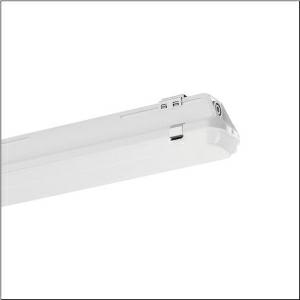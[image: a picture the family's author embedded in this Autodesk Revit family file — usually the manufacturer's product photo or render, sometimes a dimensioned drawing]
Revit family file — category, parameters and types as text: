
# Revit family: monsun_r__11_51fp108p460h_7b9f
name_source: partatom
category: Lighting Fixtures
units: mm (PartAtom-declared; Revit-internal decimal feet)

## family parameters
Cut with Voids When Loaded = No
Host = Face
Light Source = No
Part Type = Normal
Room Calculation Point = No
Round Connector Dimension = Use Diameter
Shared = No

## types (1)
- Monsun® 11 (1 x LED, 6100 lm, 33.9 W, 4000K)
    Apparent Load = 34 VA
    CIE Flux Codes = 47 77 93 94 100
    Color Rendering = 80
    Color Temperature = 4000K
    Default Elevation = 1800 mm
    Description = Monsun® 11, damp-proof luminaire, chain hanger, primary optical cover: enclosure, of PMMA, light emission: direct distribution, primary light characteristic: symmetric, installation type: suspended mounting, surface-mounted, horizontal mounting, vertical mounting, LED, rated luminous flux: 6.100lm, luminous efficacy: 180lm/W, light colour: 840, colour temperature: 4000K, control gear: ON/OFF, with terminal, 3-pole, max. 2.5mm², mains connection: 220..240V, AC, 50/60Hz, rated input power: 34W, luminaire housing, of glass-fibre reinforced polyester, uncoated, bright grey, incl. chain hanger, length: 1.590mm, width: 90mm, height: 88mm, clip for enclosure, of stainless steel (V2A), ceiling mounting element, of stainless steel (V2A), chain hanger, of stainless steel (V2A), protection rating (complete): IP66, insulation class (complete): insulation class I (protective earthing), certification: CE, ENEC, VDE, UKCA, protection symbol: D, impact resistance: IK04, permissible operating ambient temperature: -35..+40°C, standard: EN 50419, EN 60598-2-1, no direct snow, no direct sun, no direct rain, for indoor or canopied outdoor use, corresponds to IFS (International Featured Standards) requirements for safety and quality in the food industry, contact your sales advisor before using the luminaires in applications with unclear chemical exposure, large temperature fluctuations or condensation-forming humidity, LABS conformity tested according to VDMA 24364:2018-05, packaging unit: 1 piece
    Height = 89 mm
    Lamp = 1 x LED
    Lamp Light Flux = 6100 lm
    Lamp Power = 33.9 W
    Lamp count = 1
    Length = 1590 mm
    Luminous efficacy = 180 lm/W
    Manufacturer = Siteco
    ModVariant = No
    Model = 51FP108P460H
    Mounting Place = Ceiling
    Mounting Type = Surface mounted
    Number of Poles = 1
    OnlyDefault = Yes
    Power Factor = 1
    Product Name = Monsun® 11
    Product group = damp-proof luminaire
    ProductGroupID = 300
    Protection Class = Protection class I
    Protection Degree = IP 66
    RLX_Detail_Level = 1
    RLX_Emergency_Light_Flux = 0 lm
    RLX_Emergency_Type = 0
    RLX_Emergency_Type_DB = No
    RlxData = <blob elided: 88925 chars, md5=cb9cb1e1>
    Socket = socket
    Standby Power = 0 W
    System Light Flux = 6100 lm
    System Power = 34 W
    Type Comments = Product without accessories
    Type Image = l_1349237.jpg
    URL = http://relux.com
    VarID = ---
    Voltage = 0 V
    Weight = 0.00 kg
    Width = 90 mm

## geometry (parser evidence)
native form markers: Blend x4, Sweep x13
no freeform markers — native parametric forms only
